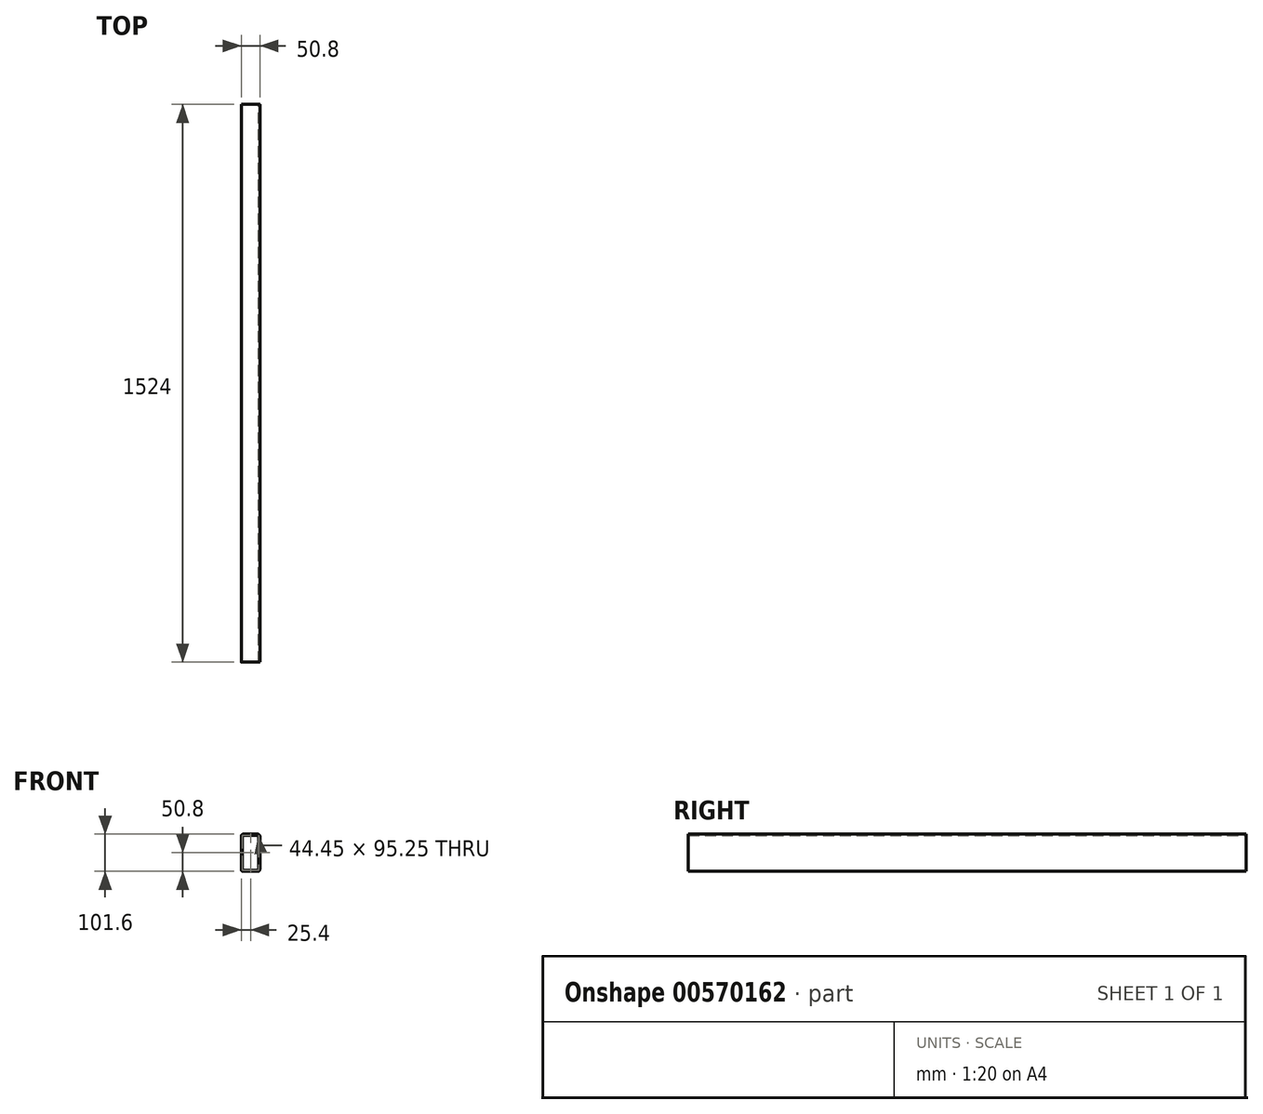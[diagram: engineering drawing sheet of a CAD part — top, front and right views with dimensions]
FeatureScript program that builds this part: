
annotation { "Feature Type Name" : "Feature", "Feature Type Description" : "" }
export const myFeature = defineFeature(function(context is Context, id is Id, definition is map)
    precondition{}
    {
        {
            var Q0;
            Q0=qCreatedBy(makeId("Front.planeOp"),FACE);
            var sketch = newSketch(context, id + "F0", { "sketchPlane" : qUnion([Q0])});
            skLineSegment(sketch, "E0.bottom", {"start": v(0, 0) * mm, "end": v(50.8, 0) * mm});
            skLineSegment(sketch, "E0.top", {"start": v(0, 101.6) * mm, "end": v(50.8, 101.6) * mm});
            skLineSegment(sketch, "E0.left", {"start": v(0, 0) * mm, "end": v(0, 101.6) * mm});
            skLineSegment(sketch, "E0.right", {"start": v(50.8, 0) * mm, "end": v(50.8, 101.6) * mm});
            skLineSegment(sketch, "E1.bottom", {"start": v(3.18, 3.17) * mm, "end": v(47.62, 3.17) * mm});
            skLineSegment(sketch, "E1.top", {"start": v(3.17, 98.43) * mm, "end": v(47.62, 98.43) * mm});
            skLineSegment(sketch, "E1.left", {"start": v(3.17, 3.18) * mm, "end": v(3.17, 98.43) * mm});
            skLineSegment(sketch, "E1.right", {"start": v(47.62, 3.18) * mm, "end": v(47.62, 98.43) * mm});
            skSolve(sketch);
        }
        {
            var Q0;
            Q0=makeQuery(id+"F0.imprint","IMPRINT",FACE,{"disambiguationData":[TD([[makeQuery(id+"F0.imprint","IMPRINT",EDGE,{"derivedFrom":sQuery(id+"F0.wireOp",EDGE,"E0.bottom")}),1.0]])]});
            extrude(context, id + "F1", {"entities" : qUnion([Q0]), "depth" : 1524 * mm, "offsetDistance" : 25.4 * mm});
        }
        {
            var Q0;
            Q0=makeQuery(id+"F1.opExtrude","SWEPT_EDGE",EDGE,{"disambiguationData":[OSD([sQuery(id+"F0.wireOp",EDGE,"E0.top"),sQuery(id+"F0.wireOp",EDGE,"E0.left")])]});
            var Q1;
            Q1=makeQuery(id+"F1.opExtrude","SWEPT_EDGE",EDGE,{"disambiguationData":[OSD([sQuery(id+"F0.wireOp",EDGE,"E0.top"),sQuery(id+"F0.wireOp",EDGE,"E0.right")])]});
            var Q2;
            Q2=makeQuery(id+"F1.opExtrude","SWEPT_EDGE",EDGE,{"disambiguationData":[OSD([sQuery(id+"F0.wireOp",EDGE,"E0.bottom"),sQuery(id+"F0.wireOp",EDGE,"E0.right")])]});
            var Q3;
            Q3=makeQuery(id+"F1.opExtrude","SWEPT_EDGE",EDGE,{"disambiguationData":[OSD([sQuery(id+"F0.wireOp",EDGE,"E0.bottom"),sQuery(id+"F0.wireOp",EDGE,"E0.left")])]});
            fillet(context, id + "F2", {"entities" : qUnion([Q0, Q1, Q2, Q3]), "radius" : 5.08 * mm, "tangentPropagation" : true, "allowEdgeOverflow" : false});
        }
    });
